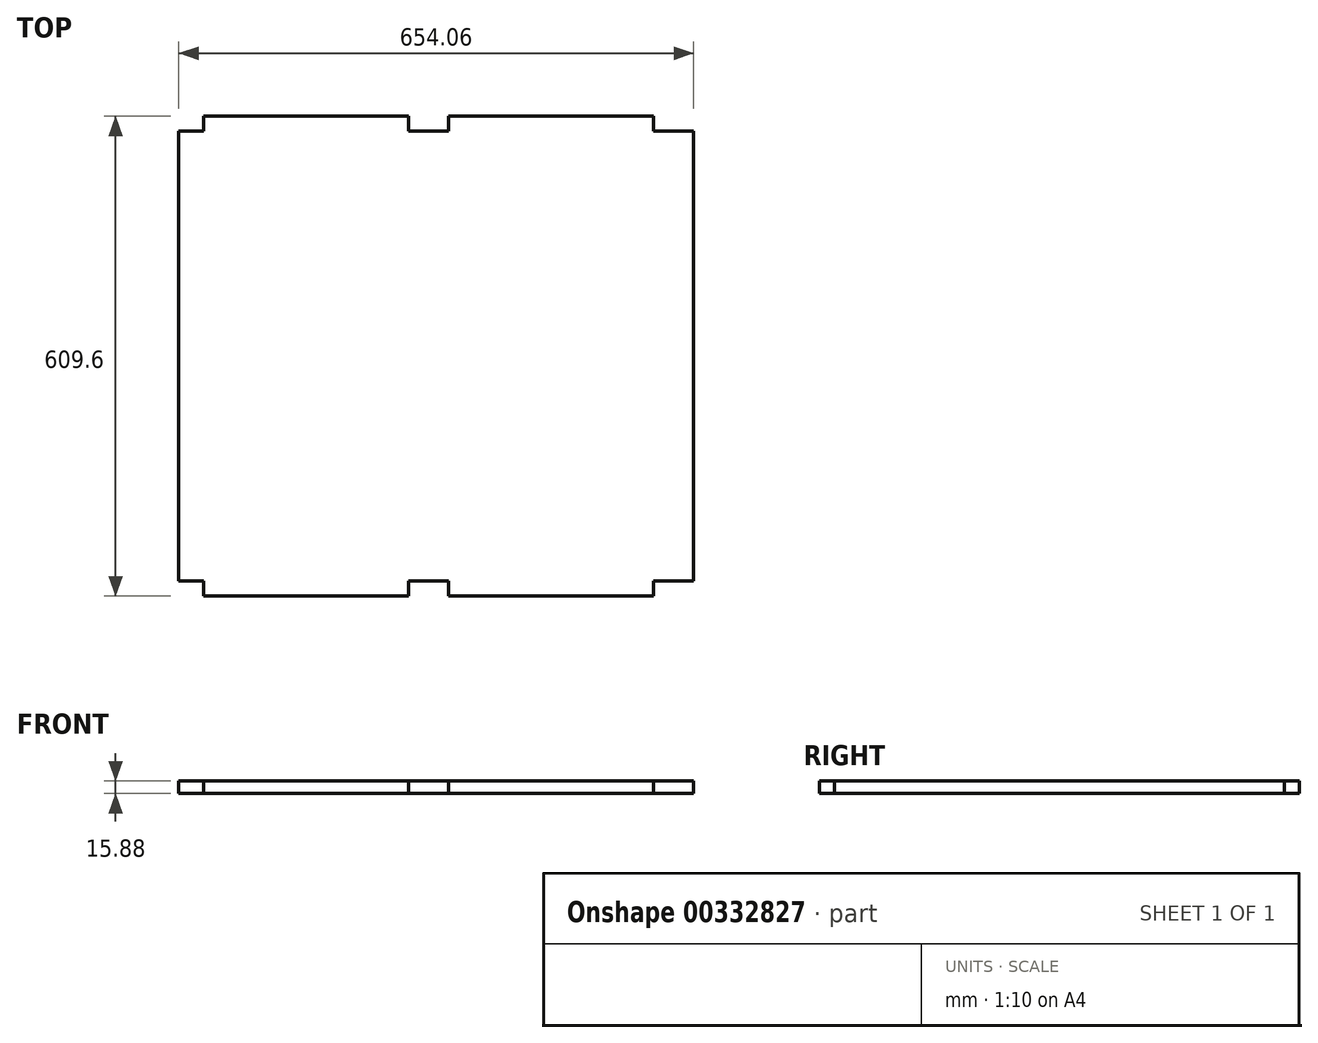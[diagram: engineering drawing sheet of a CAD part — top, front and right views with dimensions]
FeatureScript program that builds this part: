
annotation { "Feature Type Name" : "Feature", "Feature Type Description" : "" }
export const myFeature = defineFeature(function(context is Context, id is Id, definition is map)
    precondition{}
    {
        {
            var Q0;
            Q0=qCreatedBy(makeId("Top.planeOp"),FACE);
            var sketch = newSketch(context, id + "F0", { "sketchPlane" : qUnion([Q0])});
            skLineSegment(sketch, "E0.bottom", {"start": v(-295.28, -304.8) * mm, "end": v(-34.93, -304.8) * mm});
            skLineSegment(sketch, "E0.top", {"start": v(-295.27, 304.8) * mm, "end": v(-34.92, 304.8) * mm});
            skLineSegment(sketch, "E0.left", {"start": v(-327.03, -285.75) * mm, "end": v(-327.03, 285.75) * mm});
            skLineSegment(sketch, "E0.right", {"start": v(327.03, -285.75) * mm, "end": v(327.03, 285.75) * mm});
            skPoint(sketch, "E0.middle", {"position": v(0, 0) * mm});
            skLineSegment(sketch, "E1.top", {"start": v(-327.03, -285.75) * mm, "end": v(-295.28, -285.75) * mm});
            skLineSegment(sketch, "E1.right", {"start": v(-295.28, -304.8) * mm, "end": v(-295.28, -285.75) * mm});
            skPoint(sketch, "E2.orphan", {"position": v(-327.03, -304.8) * mm});
            skLineSegment(sketch, "E3.top", {"start": v(-295.27, 285.75) * mm, "end": v(-327.03, 285.75) * mm});
            skLineSegment(sketch, "E3.left", {"start": v(-295.27, 304.8) * mm, "end": v(-295.27, 285.75) * mm});
            skPoint(sketch, "E4.orphan", {"position": v(-295.27, 338.62) * mm});
            skPoint(sketch, "E5.orphan", {"position": v(-327.03, 304.8) * mm});
            skLineSegment(sketch, "E6.bottom", {"start": v(276.23, 285.75) * mm, "end": v(327.03, 285.75) * mm});
            skLineSegment(sketch, "E6.left", {"start": v(276.23, 285.75) * mm, "end": v(276.23, 304.8) * mm});
            skPoint(sketch, "E7.orphan", {"position": v(327.03, 304.8) * mm});
            skLineSegment(sketch, "E8.bottom", {"start": v(276.23, -285.75) * mm, "end": v(327.03, -285.75) * mm});
            skLineSegment(sketch, "E8.left", {"start": v(276.23, -285.75) * mm, "end": v(276.22, -304.8) * mm});
            skPoint(sketch, "E9.orphan", {"position": v(327.03, -304.8) * mm});
            skPoint(sketch, "E10.start.orphan", {"position": v(-9.52, 304.8) * mm});
            skLineSegment(sketch, "E11", {"start": v(-9.52, 304.8) * mm, "end": v(-9.53, -304.8) * mm, "construction": true});
            skLineSegment(sketch, "E12.left", {"start": v(15.88, -293.14) * mm, "end": v(15.87, -304.8) * mm, "construction": true});
            skPoint(sketch, "E12.middle", {"position": v(-9.53, -304.8) * mm});
            skPoint(sketch, "E13.orphan", {"position": v(-34.92, -285.75) * mm});
            skPoint(sketch, "E12.right.end.orphan", {"position": v(-34.93, -316.46) * mm});
            skPoint(sketch, "E14.orphan", {"position": v(15.87, -323.85) * mm});
            skLineSegment(sketch, "E15.bottom", {"start": v(-34.92, -285.75) * mm, "end": v(15.88, -285.75) * mm});
            skLineSegment(sketch, "E15.left", {"start": v(-34.92, -285.75) * mm, "end": v(-34.93, -304.8) * mm});
            skLineSegment(sketch, "E15.right", {"start": v(15.88, -285.75) * mm, "end": v(15.87, -304.8) * mm});
            skLineSegment(sketch, "E16.top", {"start": v(15.88, 285.75) * mm, "end": v(-34.92, 285.75) * mm});
            skLineSegment(sketch, "E16.left", {"start": v(15.88, 304.8) * mm, "end": v(15.88, 285.75) * mm});
            skLineSegment(sketch, "E16.right", {"start": v(-34.92, 304.8) * mm, "end": v(-34.92, 285.75) * mm});
            skPoint(sketch, "E16.bottom.end.orphan", {"position": v(-34.92, 323.85) * mm});
            skPoint(sketch, "E17.orphan", {"position": v(15.88, 323.85) * mm});
            skLineSegment(sketch, "E18.trimOffspring", {"start": v(15.88, 304.8) * mm, "end": v(276.23, 304.8) * mm});
            skLineSegment(sketch, "E19.trimOffspring", {"start": v(15.88, -304.8) * mm, "end": v(276.23, -304.8) * mm});
            skPoint(sketch, "E20.trimOffspring.end.orphan", {"position": v(-34.93, -323.85) * mm});
            skSolve(sketch);
        }
        {
            var Q0;
            Q0 = qSketchRegion(id + "F0", true);
            extrude(context, id + "F1", {"entities" : qUnion([Q0]), "depth" : 15.88 * mm});
        }
    });
